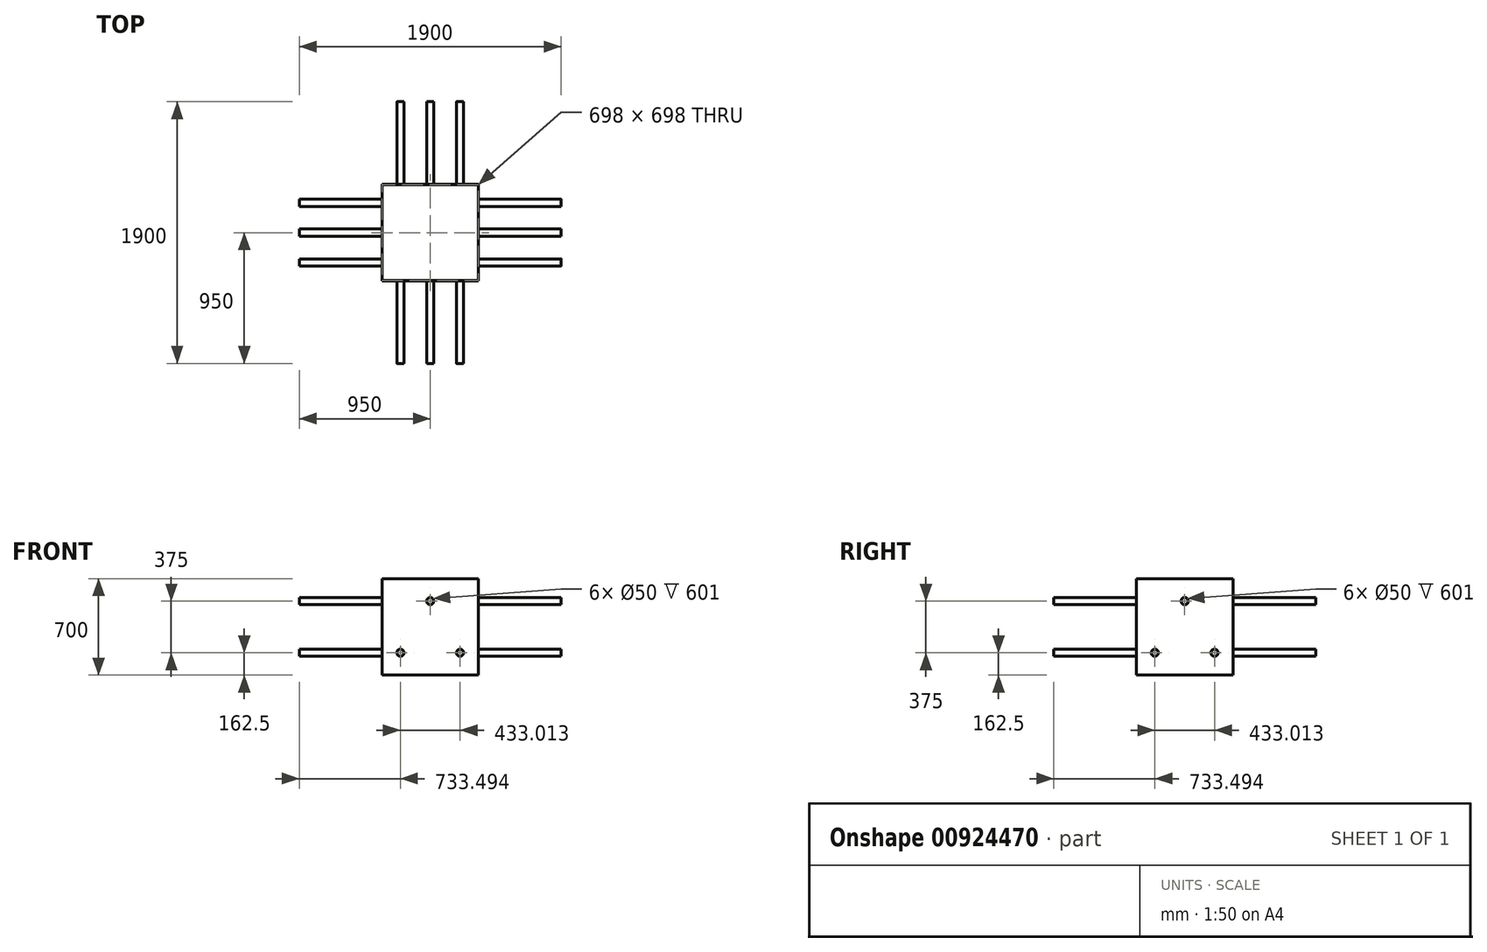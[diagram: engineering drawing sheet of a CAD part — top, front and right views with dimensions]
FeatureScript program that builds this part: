
annotation { "Feature Type Name" : "Feature", "Feature Type Description" : "" }
export const myFeature = defineFeature(function(context is Context, id is Id, definition is map)
    precondition{}
    {
        {
            var Q0;
            Q0=qCreatedBy(makeId("Top.planeOp"),FACE);
            var sketch = newSketch(context, id + "F0", { "sketchPlane" : qUnion([Q0])});
            skLineSegment(sketch, "E0.bottom", {"start": v(350, 350) * mm, "end": v(-350, 350) * mm});
            skLineSegment(sketch, "E0.top", {"start": v(350, -350) * mm, "end": v(-350, -350) * mm});
            skLineSegment(sketch, "E0.left", {"start": v(350, 350) * mm, "end": v(350, -350) * mm});
            skLineSegment(sketch, "E0.right", {"start": v(-350, 350) * mm, "end": v(-350, -350) * mm});
            skPoint(sketch, "E0.middle", {"position": v(0, 0) * mm});
            skLineSegment(sketch, "E1.bottom", {"start": v(349, 349) * mm, "end": v(-349, 349) * mm});
            skLineSegment(sketch, "E1.top", {"start": v(349, -349) * mm, "end": v(-349, -349) * mm});
            skLineSegment(sketch, "E1.left", {"start": v(349, 349) * mm, "end": v(349, -349) * mm});
            skLineSegment(sketch, "E1.right", {"start": v(-349, 349) * mm, "end": v(-349, -349) * mm});
            skLineSegment(sketch, "E2.bottom", {"start": v(-70, 70) * mm, "end": v(70, 70) * mm});
            skLineSegment(sketch, "E2.top", {"start": v(-70, -70) * mm, "end": v(70, -70) * mm});
            skLineSegment(sketch, "E2.left", {"start": v(-70, 70) * mm, "end": v(-70, -70) * mm});
            skLineSegment(sketch, "E2.right", {"start": v(70, 70) * mm, "end": v(70, -70) * mm});
            skSolve(sketch);
        }
        {
            var Q0;
            Q0=makeQuery(id+"F0.imprint","IMPRINT",FACE,{"disambiguationData":[TD([[makeQuery(id+"F0.imprint","IMPRINT",EDGE,{"derivedFrom":sQuery(id+"F0.wireOp",EDGE,"E0.bottom")}),1.0]])]});
            extrude(context, id + "F1", {"entities" : qUnion([Q0]), "oppositeDirection" : true, "depth" : 700 * mm, "offsetDistance" : 25 * mm});
        }
        {
            var Q0;
            Q0=makeQuery(id+"F1.opExtrude","SWEPT_FACE",FACE,{"disambiguationData":[OSD([sQuery(id+"F0.wireOp",EDGE,"E0.left")])]});
            var sketch = newSketch(context, id + "F2", { "sketchPlane" : qUnion([Q0])});
            skPoint(sketch, "E3", {"position": v(0, -350) * mm});
            skPoint(sketch, "E3.positionSnap0", {"position": v(-350, -350) * mm});
            skPoint(sketch, "E3.positionSnap1", {"position": v(0, 0) * mm});
            skCircle(sketch, "E4.cCircle", {"center": v(0, -412.5) * mm, "radius": 250 * mm, "construction": true});
            skLineSegment(sketch, "E4.0", {"start": v(0, -162.5) * mm, "end": v(216.5, -537.5) * mm});
            skLineSegment(sketch, "E4.1", {"start": v(216.5, -537.5) * mm, "end": v(-216.5, -537.5) * mm});
            skLineSegment(sketch, "E4.2", {"start": v(-216.5, -537.5) * mm, "end": v(0, -162.5) * mm});
            skCircle(sketch, "E5", {"center": v(0, -162.5) * mm, "radius": 25 * mm});
            skCircle(sketch, "E6", {"center": v(216.5, -537.5) * mm, "radius": 25 * mm});
            skCircle(sketch, "E7", {"center": v(-216.5, -537.5) * mm, "radius": 25 * mm});
            skCircle(sketch, "E8", {"center": v(0, -162.5) * mm, "radius": 26 * mm});
            skCircle(sketch, "E9", {"center": v(-216.5, -537.5) * mm, "radius": 26 * mm});
            skCircle(sketch, "E10", {"center": v(216.5, -537.5) * mm, "radius": 26 * mm});
            skSolve(sketch);
        }
        {
            var Q0;
            Q0=makeQuery(id+"F1.opExtrude","SWEPT_FACE",FACE,{"disambiguationData":[OSD([sQuery(id+"F0.wireOp",EDGE,"E0.top")])]});
            var sketch = newSketch(context, id + "F3", { "sketchPlane" : qUnion([Q0])});
            skPoint(sketch, "E11", {"position": v(0, -412.5) * mm});
            skPoint(sketch, "E11.positionSnap0", {"position": v(-350, -412.5) * mm});
            skPoint(sketch, "E11.positionSnap1", {"position": v(0, 157.53) * mm});
            skCircle(sketch, "E12.cCircle", {"center": v(0, -412.5) * mm, "radius": 250 * mm, "construction": true});
            skLineSegment(sketch, "E12.0", {"start": v(0, -162.5) * mm, "end": v(216.5, -537.5) * mm});
            skLineSegment(sketch, "E12.1", {"start": v(216.5, -537.5) * mm, "end": v(-216.5, -537.5) * mm});
            skLineSegment(sketch, "E12.2", {"start": v(-216.5, -537.5) * mm, "end": v(0, -162.5) * mm});
            skCircle(sketch, "E13", {"center": v(0, -162.5) * mm, "radius": 25 * mm});
            skCircle(sketch, "E14", {"center": v(216.5, -537.5) * mm, "radius": 25 * mm});
            skCircle(sketch, "E15", {"center": v(-216.5, -537.5) * mm, "radius": 25 * mm});
            skCircle(sketch, "E16", {"center": v(0, -162.5) * mm, "radius": 26 * mm});
            skCircle(sketch, "E17", {"center": v(-216.5, -537.5) * mm, "radius": 26 * mm});
            skCircle(sketch, "E18", {"center": v(216.5, -537.5) * mm, "radius": 26 * mm});
            skSolve(sketch);
        }
        {
            var Q0;
            Q0=makeQuery(id+"F1.opExtrude","SWEPT_FACE",FACE,{"disambiguationData":[OSD([sQuery(id+"F0.wireOp",EDGE,"E0.right")])]});
            var sketch = newSketch(context, id + "F4", { "sketchPlane" : qUnion([Q0])});
            skPoint(sketch, "E19", {"position": v(0, -350) * mm});
            skPoint(sketch, "E19.positionSnap0", {"position": v(-350, -350) * mm});
            skPoint(sketch, "E19.positionSnap1", {"position": v(0, 0) * mm});
            skCircle(sketch, "E20.cCircle", {"center": v(0, -412.5) * mm, "radius": 250 * mm, "construction": true});
            skLineSegment(sketch, "E20.0", {"start": v(0, -162.5) * mm, "end": v(216.5, -537.5) * mm});
            skLineSegment(sketch, "E20.1", {"start": v(216.5, -537.5) * mm, "end": v(-216.5, -537.5) * mm});
            skLineSegment(sketch, "E20.2", {"start": v(-216.5, -537.5) * mm, "end": v(0, -162.5) * mm});
            skCircle(sketch, "E21", {"center": v(0, -162.5) * mm, "radius": 25 * mm});
            skCircle(sketch, "E22", {"center": v(216.5, -537.5) * mm, "radius": 25 * mm});
            skCircle(sketch, "E23", {"center": v(-216.5, -537.5) * mm, "radius": 25 * mm});
            skCircle(sketch, "E24", {"center": v(0, -162.5) * mm, "radius": 26 * mm});
            skCircle(sketch, "E25", {"center": v(-216.5, -537.5) * mm, "radius": 26 * mm});
            skCircle(sketch, "E26", {"center": v(216.5, -537.5) * mm, "radius": 26 * mm});
            skSolve(sketch);
        }
        {
            var Q0;
            Q0=makeQuery(id+"F1.opExtrude","SWEPT_FACE",FACE,{"disambiguationData":[OSD([sQuery(id+"F0.wireOp",EDGE,"E0.bottom")])]});
            var sketch = newSketch(context, id + "F5", { "sketchPlane" : qUnion([Q0])});
            skPoint(sketch, "E27", {"position": v(0, -350) * mm});
            skPoint(sketch, "E27.positionSnap0", {"position": v(-350, -350) * mm});
            skPoint(sketch, "E27.positionSnap1", {"position": v(0, 0) * mm});
            skCircle(sketch, "E28.cCircle", {"center": v(0, -412.5) * mm, "radius": 250 * mm, "construction": true});
            skLineSegment(sketch, "E28.0", {"start": v(0, -162.5) * mm, "end": v(216.5, -537.5) * mm});
            skLineSegment(sketch, "E28.1", {"start": v(216.5, -537.5) * mm, "end": v(-216.5, -537.5) * mm});
            skLineSegment(sketch, "E28.2", {"start": v(-216.5, -537.5) * mm, "end": v(0, -162.5) * mm});
            skCircle(sketch, "E29", {"center": v(0, -162.5) * mm, "radius": 25 * mm});
            skCircle(sketch, "E30", {"center": v(216.5, -537.5) * mm, "radius": 25 * mm});
            skCircle(sketch, "E31", {"center": v(-216.5, -537.5) * mm, "radius": 25 * mm});
            skCircle(sketch, "E32", {"center": v(0, -162.5) * mm, "radius": 26 * mm});
            skCircle(sketch, "E33", {"center": v(216.5, -537.5) * mm, "radius": 26 * mm});
            skCircle(sketch, "E34", {"center": v(-216.5, -537.5) * mm, "radius": 26 * mm});
            skSolve(sketch);
        }
        {
            var Q0;
            {var subQ0=sQuery(id+"F2.wireOp",EDGE,"E5");var subQ1=sQuery(id+"F2.wireOp",EDGE,"E4.0");var subQ2=makeQuery(id+"F2.imprint","INTERSECT",VERTEX,{"derivedFrom":[subQ1,subQ0]});Q0=makeQuery(id+"F2.imprint","IMPRINT",FACE,{"disambiguationData":[TD([[makeQuery(id+"F2.imprint","IMPRINT",EDGE,{"disambiguationData":[TD([[subQ2,-1.0]])],"derivedFrom":subQ1}),1.0]])]});}
            var Q1;
            {var subQ0=sQuery(id+"F2.wireOp",EDGE,"E10");var subQ1=sQuery(id+"F2.wireOp",EDGE,"E4.0");var subQ2=makeQuery(id+"F2.imprint","INTERSECT",VERTEX,{"derivedFrom":[subQ1,subQ0]});Q1=makeQuery(id+"F2.imprint","IMPRINT",FACE,{"disambiguationData":[TD([[makeQuery(id+"F2.imprint","IMPRINT",EDGE,{"disambiguationData":[TD([[subQ2,-1.0]])],"derivedFrom":subQ1}),1.0]])]});}
            var Q2;
            {var subQ0=sQuery(id+"F2.wireOp",EDGE,"E10");var subQ1=sQuery(id+"F2.wireOp",EDGE,"E4.0");var subQ2=makeQuery(id+"F2.imprint","INTERSECT",VERTEX,{"derivedFrom":[subQ1,subQ0]});Q2=makeQuery(id+"F2.imprint","IMPRINT",FACE,{"disambiguationData":[TD([[makeQuery(id+"F2.imprint","IMPRINT",EDGE,{"disambiguationData":[TD([[subQ2,-1.0]])],"derivedFrom":subQ1}),-1.0]])]});}
            var Q3;
            {var subQ0=sQuery(id+"F2.wireOp",EDGE,"E5");var subQ1=sQuery(id+"F2.wireOp",EDGE,"E4.0");var subQ2=makeQuery(id+"F2.imprint","INTERSECT",VERTEX,{"derivedFrom":[subQ1,subQ0]});Q3=makeQuery(id+"F2.imprint","IMPRINT",FACE,{"disambiguationData":[TD([[makeQuery(id+"F2.imprint","IMPRINT",EDGE,{"disambiguationData":[TD([[subQ2,-1.0]])],"derivedFrom":subQ1}),-1.0]])]});}
            var Q4;
            {var subQ0=sQuery(id+"F2.wireOp",EDGE,"E9");var subQ1=sQuery(id+"F2.wireOp",EDGE,"E4.1");var subQ2=makeQuery(id+"F2.imprint","INTERSECT",VERTEX,{"derivedFrom":[subQ1,subQ0]});Q4=makeQuery(id+"F2.imprint","IMPRINT",FACE,{"disambiguationData":[TD([[makeQuery(id+"F2.imprint","IMPRINT",EDGE,{"disambiguationData":[TD([[subQ2,-1.0]])],"derivedFrom":subQ1}),1.0]])]});}
            var Q5;
            {var subQ0=sQuery(id+"F2.wireOp",EDGE,"E9");var subQ1=sQuery(id+"F2.wireOp",EDGE,"E4.1");var subQ2=makeQuery(id+"F2.imprint","INTERSECT",VERTEX,{"derivedFrom":[subQ1,subQ0]});Q5=makeQuery(id+"F2.imprint","IMPRINT",FACE,{"disambiguationData":[TD([[makeQuery(id+"F2.imprint","IMPRINT",EDGE,{"disambiguationData":[TD([[subQ2,-1.0]])],"derivedFrom":subQ1}),-1.0]])]});}
            extrude(context, id + "F6", {"entities" : qUnion([Q0, Q1, Q2, Q3, Q4, Q5]), "operationType" : NewBodyOperationType.ADD, "depth" : 600 * mm, "offsetDistance" : 25 * mm});
        }
        {
            var Q0;
            {var subQ0=sQuery(id+"F3.wireOp",EDGE,"E13");var subQ1=sQuery(id+"F3.wireOp",EDGE,"E12.0");var subQ2=makeQuery(id+"F3.imprint","INTERSECT",VERTEX,{"derivedFrom":[subQ1,subQ0]});Q0=makeQuery(id+"F3.imprint","IMPRINT",FACE,{"disambiguationData":[TD([[makeQuery(id+"F3.imprint","IMPRINT",EDGE,{"disambiguationData":[TD([[subQ2,-1.0]])],"derivedFrom":subQ1}),-1.0]])]});}
            var Q1;
            {var subQ0=sQuery(id+"F3.wireOp",EDGE,"E13");var subQ1=sQuery(id+"F3.wireOp",EDGE,"E12.0");var subQ2=makeQuery(id+"F3.imprint","INTERSECT",VERTEX,{"derivedFrom":[subQ1,subQ0]});Q1=makeQuery(id+"F3.imprint","IMPRINT",FACE,{"disambiguationData":[TD([[makeQuery(id+"F3.imprint","IMPRINT",EDGE,{"disambiguationData":[TD([[subQ2,-1.0]])],"derivedFrom":subQ1}),1.0]])]});}
            var Q2;
            {var subQ0=sQuery(id+"F3.wireOp",EDGE,"E17");var subQ1=sQuery(id+"F3.wireOp",EDGE,"E12.1");var subQ2=makeQuery(id+"F3.imprint","INTERSECT",VERTEX,{"derivedFrom":[subQ1,subQ0]});Q2=makeQuery(id+"F3.imprint","IMPRINT",FACE,{"disambiguationData":[TD([[makeQuery(id+"F3.imprint","IMPRINT",EDGE,{"disambiguationData":[TD([[subQ2,-1.0]])],"derivedFrom":subQ1}),1.0]])]});}
            var Q3;
            {var subQ0=sQuery(id+"F3.wireOp",EDGE,"E17");var subQ1=sQuery(id+"F3.wireOp",EDGE,"E12.1");var subQ2=makeQuery(id+"F3.imprint","INTERSECT",VERTEX,{"derivedFrom":[subQ1,subQ0]});Q3=makeQuery(id+"F3.imprint","IMPRINT",FACE,{"disambiguationData":[TD([[makeQuery(id+"F3.imprint","IMPRINT",EDGE,{"disambiguationData":[TD([[subQ2,-1.0]])],"derivedFrom":subQ1}),-1.0]])]});}
            var Q4;
            {var subQ0=sQuery(id+"F3.wireOp",EDGE,"E18");var subQ1=sQuery(id+"F3.wireOp",EDGE,"E12.0");var subQ2=makeQuery(id+"F3.imprint","INTERSECT",VERTEX,{"derivedFrom":[subQ1,subQ0]});Q4=makeQuery(id+"F3.imprint","IMPRINT",FACE,{"disambiguationData":[TD([[makeQuery(id+"F3.imprint","IMPRINT",EDGE,{"disambiguationData":[TD([[subQ2,-1.0]])],"derivedFrom":subQ1}),1.0]])]});}
            var Q5;
            {var subQ0=sQuery(id+"F3.wireOp",EDGE,"E18");var subQ1=sQuery(id+"F3.wireOp",EDGE,"E12.0");var subQ2=makeQuery(id+"F3.imprint","INTERSECT",VERTEX,{"derivedFrom":[subQ1,subQ0]});Q5=makeQuery(id+"F3.imprint","IMPRINT",FACE,{"disambiguationData":[TD([[makeQuery(id+"F3.imprint","IMPRINT",EDGE,{"disambiguationData":[TD([[subQ2,-1.0]])],"derivedFrom":subQ1}),-1.0]])]});}
            extrude(context, id + "F7", {"entities" : qUnion([Q0, Q1, Q2, Q3, Q4, Q5]), "operationType" : NewBodyOperationType.ADD, "depth" : 600 * mm, "offsetDistance" : 25 * mm});
        }
        {
            var Q0;
            {var subQ0=sQuery(id+"F4.wireOp",EDGE,"E21");var subQ1=sQuery(id+"F4.wireOp",EDGE,"E20.0");var subQ2=makeQuery(id+"F4.imprint","INTERSECT",VERTEX,{"derivedFrom":[subQ1,subQ0]});Q0=makeQuery(id+"F4.imprint","IMPRINT",FACE,{"disambiguationData":[TD([[makeQuery(id+"F4.imprint","IMPRINT",EDGE,{"disambiguationData":[TD([[subQ2,-1.0]])],"derivedFrom":subQ1}),1.0]])]});}
            var Q1;
            {var subQ0=sQuery(id+"F4.wireOp",EDGE,"E21");var subQ1=sQuery(id+"F4.wireOp",EDGE,"E20.0");var subQ2=makeQuery(id+"F4.imprint","INTERSECT",VERTEX,{"derivedFrom":[subQ1,subQ0]});Q1=makeQuery(id+"F4.imprint","IMPRINT",FACE,{"disambiguationData":[TD([[makeQuery(id+"F4.imprint","IMPRINT",EDGE,{"disambiguationData":[TD([[subQ2,-1.0]])],"derivedFrom":subQ1}),-1.0]])]});}
            var Q2;
            {var subQ0=sQuery(id+"F4.wireOp",EDGE,"E26");var subQ1=sQuery(id+"F4.wireOp",EDGE,"E20.0");var subQ2=makeQuery(id+"F4.imprint","INTERSECT",VERTEX,{"derivedFrom":[subQ1,subQ0]});Q2=makeQuery(id+"F4.imprint","IMPRINT",FACE,{"disambiguationData":[TD([[makeQuery(id+"F4.imprint","IMPRINT",EDGE,{"disambiguationData":[TD([[subQ2,-1.0]])],"derivedFrom":subQ1}),1.0]])]});}
            var Q3;
            {var subQ0=sQuery(id+"F4.wireOp",EDGE,"E26");var subQ1=sQuery(id+"F4.wireOp",EDGE,"E20.0");var subQ2=makeQuery(id+"F4.imprint","INTERSECT",VERTEX,{"derivedFrom":[subQ1,subQ0]});Q3=makeQuery(id+"F4.imprint","IMPRINT",FACE,{"disambiguationData":[TD([[makeQuery(id+"F4.imprint","IMPRINT",EDGE,{"disambiguationData":[TD([[subQ2,-1.0]])],"derivedFrom":subQ1}),-1.0]])]});}
            var Q4;
            {var subQ0=sQuery(id+"F4.wireOp",EDGE,"E25");var subQ1=sQuery(id+"F4.wireOp",EDGE,"E20.1");var subQ2=makeQuery(id+"F4.imprint","INTERSECT",VERTEX,{"derivedFrom":[subQ1,subQ0]});Q4=makeQuery(id+"F4.imprint","IMPRINT",FACE,{"disambiguationData":[TD([[makeQuery(id+"F4.imprint","IMPRINT",EDGE,{"disambiguationData":[TD([[subQ2,-1.0]])],"derivedFrom":subQ1}),1.0]])]});}
            var Q5;
            {var subQ0=sQuery(id+"F4.wireOp",EDGE,"E25");var subQ1=sQuery(id+"F4.wireOp",EDGE,"E20.1");var subQ2=makeQuery(id+"F4.imprint","INTERSECT",VERTEX,{"derivedFrom":[subQ1,subQ0]});Q5=makeQuery(id+"F4.imprint","IMPRINT",FACE,{"disambiguationData":[TD([[makeQuery(id+"F4.imprint","IMPRINT",EDGE,{"disambiguationData":[TD([[subQ2,-1.0]])],"derivedFrom":subQ1}),-1.0]])]});}
            extrude(context, id + "F8", {"entities" : qUnion([Q0, Q1, Q2, Q3, Q4, Q5]), "operationType" : NewBodyOperationType.ADD, "depth" : 600 * mm, "offsetDistance" : 25 * mm});
        }
        {
            var Q0;
            {var subQ0=sQuery(id+"F5.wireOp",EDGE,"E29");var subQ1=sQuery(id+"F5.wireOp",EDGE,"E28.0");var subQ2=makeQuery(id+"F5.imprint","INTERSECT",VERTEX,{"derivedFrom":[subQ1,subQ0]});Q0=makeQuery(id+"F5.imprint","IMPRINT",FACE,{"disambiguationData":[TD([[makeQuery(id+"F5.imprint","IMPRINT",EDGE,{"disambiguationData":[TD([[subQ2,-1.0]])],"derivedFrom":subQ1}),-1.0]])]});}
            var Q1;
            {var subQ0=sQuery(id+"F5.wireOp",EDGE,"E29");var subQ1=sQuery(id+"F5.wireOp",EDGE,"E28.0");var subQ2=makeQuery(id+"F5.imprint","INTERSECT",VERTEX,{"derivedFrom":[subQ1,subQ0]});Q1=makeQuery(id+"F5.imprint","IMPRINT",FACE,{"disambiguationData":[TD([[makeQuery(id+"F5.imprint","IMPRINT",EDGE,{"disambiguationData":[TD([[subQ2,-1.0]])],"derivedFrom":subQ1}),1.0]])]});}
            var Q2;
            {var subQ0=sQuery(id+"F5.wireOp",EDGE,"E34");var subQ1=sQuery(id+"F5.wireOp",EDGE,"E28.1");var subQ2=makeQuery(id+"F5.imprint","INTERSECT",VERTEX,{"derivedFrom":[subQ1,subQ0]});Q2=makeQuery(id+"F5.imprint","IMPRINT",FACE,{"disambiguationData":[TD([[makeQuery(id+"F5.imprint","IMPRINT",EDGE,{"disambiguationData":[TD([[subQ2,-1.0]])],"derivedFrom":subQ1}),1.0]])]});}
            var Q3;
            {var subQ0=sQuery(id+"F5.wireOp",EDGE,"E34");var subQ1=sQuery(id+"F5.wireOp",EDGE,"E28.1");var subQ2=makeQuery(id+"F5.imprint","INTERSECT",VERTEX,{"derivedFrom":[subQ1,subQ0]});Q3=makeQuery(id+"F5.imprint","IMPRINT",FACE,{"disambiguationData":[TD([[makeQuery(id+"F5.imprint","IMPRINT",EDGE,{"disambiguationData":[TD([[subQ2,-1.0]])],"derivedFrom":subQ1}),-1.0]])]});}
            var Q4;
            {var subQ0=sQuery(id+"F5.wireOp",EDGE,"E33");var subQ1=sQuery(id+"F5.wireOp",EDGE,"E28.0");var subQ2=makeQuery(id+"F5.imprint","INTERSECT",VERTEX,{"derivedFrom":[subQ1,subQ0]});Q4=makeQuery(id+"F5.imprint","IMPRINT",FACE,{"disambiguationData":[TD([[makeQuery(id+"F5.imprint","IMPRINT",EDGE,{"disambiguationData":[TD([[subQ2,-1.0]])],"derivedFrom":subQ1}),-1.0]])]});}
            var Q5;
            {var subQ0=sQuery(id+"F5.wireOp",EDGE,"E33");var subQ1=sQuery(id+"F5.wireOp",EDGE,"E28.0");var subQ2=makeQuery(id+"F5.imprint","INTERSECT",VERTEX,{"derivedFrom":[subQ1,subQ0]});Q5=makeQuery(id+"F5.imprint","IMPRINT",FACE,{"disambiguationData":[TD([[makeQuery(id+"F5.imprint","IMPRINT",EDGE,{"disambiguationData":[TD([[subQ2,-1.0]])],"derivedFrom":subQ1}),1.0]])]});}
            extrude(context, id + "F9", {"entities" : qUnion([Q0, Q1, Q2, Q3, Q4, Q5]), "operationType" : NewBodyOperationType.ADD, "depth" : 600 * mm, "offsetDistance" : 25 * mm});
        }
        {
            var Q0;
            Q0=makeQuery(id+"F6.boolean.opBoolean","SPLIT",FACE,{"disambiguationData":[TD([makeQuery(id+"F6.opExtrude","SWEPT_FACE",FACE,{"disambiguationData":[OSD([sQuery(id+"F2.wireOp",EDGE,"E7")])]})])],"derivedFrom":makeQuery(id+"F1.opExtrude","SWEPT_FACE",FACE,{"disambiguationData":[OSD([sQuery(id+"F0.wireOp",EDGE,"E0.left")])]})});
            extrude(context, id + "F10", {"entities" : qUnion([Q0]), "operationType" : NewBodyOperationType.REMOVE, "oppositeDirection" : true, "depth" : 25 * mm, "offsetDistance" : 25 * mm});
        }
        {
            var Q0;
            Q0=makeQuery(id+"F6.boolean.opBoolean","SPLIT",FACE,{"disambiguationData":[TD([makeQuery(id+"F6.opExtrude","SWEPT_FACE",FACE,{"disambiguationData":[OSD([sQuery(id+"F2.wireOp",EDGE,"E6")])]})])],"derivedFrom":makeQuery(id+"F1.opExtrude","SWEPT_FACE",FACE,{"disambiguationData":[OSD([sQuery(id+"F0.wireOp",EDGE,"E0.left")])]})});
            extrude(context, id + "F11", {"entities" : qUnion([Q0]), "operationType" : NewBodyOperationType.REMOVE, "oppositeDirection" : true, "depth" : 25 * mm, "offsetDistance" : 25 * mm});
        }
        {
            var Q0;
            Q0=makeQuery(id+"F8.boolean.opBoolean","SPLIT",FACE,{"disambiguationData":[TD([makeQuery(id+"F8.opExtrude","SWEPT_FACE",FACE,{"disambiguationData":[OSD([sQuery(id+"F4.wireOp",EDGE,"E23")])]})])],"derivedFrom":makeQuery(id+"F1.opExtrude","SWEPT_FACE",FACE,{"disambiguationData":[OSD([sQuery(id+"F0.wireOp",EDGE,"E0.right")])]})});
            extrude(context, id + "F12", {"entities" : qUnion([Q0]), "operationType" : NewBodyOperationType.REMOVE, "oppositeDirection" : true, "depth" : 25 * mm, "offsetDistance" : 25 * mm});
        }
        {
            var Q0;
            Q0=makeQuery(id+"F8.boolean.opBoolean","SPLIT",FACE,{"disambiguationData":[TD([makeQuery(id+"F8.opExtrude","SWEPT_FACE",FACE,{"disambiguationData":[OSD([sQuery(id+"F4.wireOp",EDGE,"E22")])]})])],"derivedFrom":makeQuery(id+"F1.opExtrude","SWEPT_FACE",FACE,{"disambiguationData":[OSD([sQuery(id+"F0.wireOp",EDGE,"E0.right")])]})});
            extrude(context, id + "F13", {"entities" : qUnion([Q0]), "operationType" : NewBodyOperationType.REMOVE, "oppositeDirection" : true, "depth" : 25 * mm, "offsetDistance" : 25 * mm});
        }
        {
            var Q0;
            Q0=makeQuery(id+"F9.boolean.opBoolean","SPLIT",FACE,{"disambiguationData":[TD([makeQuery(id+"F9.opExtrude","SWEPT_FACE",FACE,{"disambiguationData":[OSD([sQuery(id+"F5.wireOp",EDGE,"E30")])]})])],"derivedFrom":makeQuery(id+"F1.opExtrude","SWEPT_FACE",FACE,{"disambiguationData":[OSD([sQuery(id+"F0.wireOp",EDGE,"E0.bottom")])]})});
            var Q1;
            Q1=makeQuery(id+"F9.boolean.opBoolean","SPLIT",FACE,{"disambiguationData":[TD([makeQuery(id+"F9.opExtrude","SWEPT_FACE",FACE,{"disambiguationData":[OSD([sQuery(id+"F5.wireOp",EDGE,"E31")])]})])],"derivedFrom":makeQuery(id+"F1.opExtrude","SWEPT_FACE",FACE,{"disambiguationData":[OSD([sQuery(id+"F0.wireOp",EDGE,"E0.bottom")])]})});
            extrude(context, id + "F14", {"entities" : qUnion([Q0, Q1]), "operationType" : NewBodyOperationType.REMOVE, "oppositeDirection" : true, "depth" : 25 * mm, "offsetDistance" : 25 * mm});
        }
        {
            var Q0;
            Q0=makeQuery(id+"F7.boolean.opBoolean","SPLIT",FACE,{"disambiguationData":[TD([makeQuery(id+"F7.opExtrude","SWEPT_FACE",FACE,{"disambiguationData":[OSD([sQuery(id+"F3.wireOp",EDGE,"E14")])]})])],"derivedFrom":makeQuery(id+"F1.opExtrude","SWEPT_FACE",FACE,{"disambiguationData":[OSD([sQuery(id+"F0.wireOp",EDGE,"E0.top")])]})});
            var Q1;
            Q1=makeQuery(id+"F7.boolean.opBoolean","SPLIT",FACE,{"disambiguationData":[TD([makeQuery(id+"F7.opExtrude","SWEPT_FACE",FACE,{"disambiguationData":[OSD([sQuery(id+"F3.wireOp",EDGE,"E15")])]})])],"derivedFrom":makeQuery(id+"F1.opExtrude","SWEPT_FACE",FACE,{"disambiguationData":[OSD([sQuery(id+"F0.wireOp",EDGE,"E0.top")])]})});
            extrude(context, id + "F15", {"entities" : qUnion([Q0, Q1]), "operationType" : NewBodyOperationType.REMOVE, "oppositeDirection" : true, "depth" : 25 * mm, "offsetDistance" : 25 * mm});
        }
        {
            var Q0;
            Q0=makeQuery(id+"F6.boolean.opBoolean","SPLIT",FACE,{"disambiguationData":[TD([makeQuery(id+"F6.opExtrude","SWEPT_FACE",FACE,{"disambiguationData":[OSD([sQuery(id+"F2.wireOp",EDGE,"E5")])]})])],"derivedFrom":makeQuery(id+"F1.opExtrude","SWEPT_FACE",FACE,{"disambiguationData":[OSD([sQuery(id+"F0.wireOp",EDGE,"E0.left")])]})});
            extrude(context, id + "F16", {"entities" : qUnion([Q0]), "operationType" : NewBodyOperationType.REMOVE, "oppositeDirection" : true, "depth" : 4990 * mm, "offsetDistance" : 25 * mm});
        }
        {
            var Q0;
            Q0=makeQuery(id+"F9.boolean.opBoolean","SPLIT",FACE,{"disambiguationData":[TD([makeQuery(id+"F9.opExtrude","SWEPT_FACE",FACE,{"disambiguationData":[OSD([sQuery(id+"F5.wireOp",EDGE,"E29")])]})])],"derivedFrom":makeQuery(id+"F1.opExtrude","SWEPT_FACE",FACE,{"disambiguationData":[OSD([sQuery(id+"F0.wireOp",EDGE,"E0.bottom")])]})});
            extrude(context, id + "F17", {"entities" : qUnion([Q0]), "operationType" : NewBodyOperationType.REMOVE, "oppositeDirection" : true, "depth" : 4980 * mm, "offsetDistance" : 25 * mm});
        }
    });
